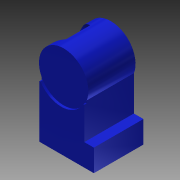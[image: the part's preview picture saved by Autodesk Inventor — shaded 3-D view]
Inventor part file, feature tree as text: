
AUTODESK INVENTOR PART (.ipt)
format: ipt  version: 2015 (Build 190159000, 159)  size: 148,480 bytes
history: native  units: mm
features: extrude x5, sketch x5, fillet x1
ambient origin geometry x8: Origin, YZ Plane, XZ Plane, XY Plane, X Axis, Y Axis, Z Axis, Center Point
bodies: Solid1 (feature_tree)
feature tree (11):
  extrude  "Extrusion1"  Depth=7.83mm
  extrude  "Extrusion2"  Depth=3.54mm
  extrude  "Extrusion3"  Depth=6.457mm
  extrude  "Extrusion4"  Depth=5.0mm
  extrude  "Extrusion6"  Depth=2.0mm TaperAngle=0.0deg
  fillet  "Fillet2"  Radius=5.0mm
  sketch  "Sketch1"  dims[d0=7.83mm d1=9.45mm]
  sketch  "Sketch2"  dims[d2=3.54mm d3=3.154mm]
  sketch  "Sketch3"  dims[d4=3.171mm d5=6.457mm]
  sketch  "Sketch4"  dims[d6=7.108mm d7=0.0mm d8=5.0mm]
  sketch  "Sketch6"  dims[d9=3.2mm d10=2.0mm d11=0.0mm d12=5.0mm d13=3.0mm d14=2.0mm d15=0.0mm d16=8.0mm d17=2.0mm d18=0.0mm d22=0.345mm d23=0.0mm d24=0.1mm]
